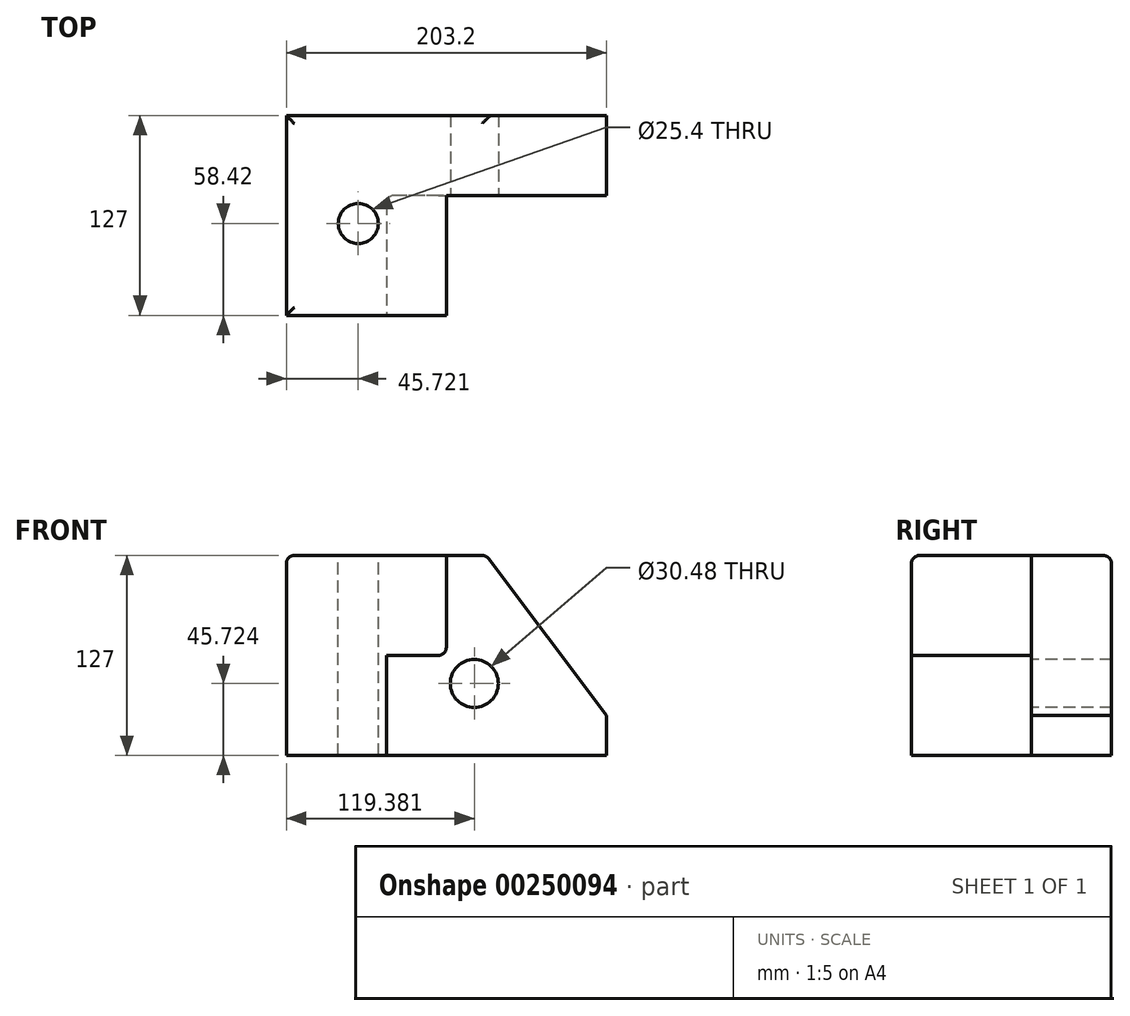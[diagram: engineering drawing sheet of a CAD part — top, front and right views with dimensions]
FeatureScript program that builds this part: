
annotation { "Feature Type Name" : "Feature", "Feature Type Description" : "" }
export const myFeature = defineFeature(function(context is Context, id is Id, definition is map)
    precondition{}
    {
        {
            var Q0;
            Q0=qCreatedBy(makeId("Front.planeOp"),FACE);
            var sketch = newSketch(context, id + "F0", { "sketchPlane" : qUnion([Q0])});
            skLineSegment(sketch, "E0.bottom", {"start": v(67.15, -74.26) * mm, "end": v(-136.05, -74.26) * mm});
            skLineSegment(sketch, "E0.top", {"start": v(67.15, 52.74) * mm, "end": v(-136.05, 52.74) * mm});
            skLineSegment(sketch, "E0.left", {"start": v(67.15, -74.26) * mm, "end": v(67.15, 52.74) * mm});
            skLineSegment(sketch, "E0.right", {"start": v(-136.05, -74.26) * mm, "end": v(-136.05, 52.74) * mm});
            skPoint(sketch, "E0.middle", {"position": v(-34.45, -10.76) * mm});
            skSolve(sketch);
        }
        {
            var Q0;
            Q0 = qSketchRegion(id + "F0", true);
            var Q1;
            Q1 = qConstructionFilter(qBodyType(qCreatedBy(id + "F0" ,EDGE), BodyType.WIRE), ConstructionObject.NO);
            extrude(context, id + "F1", {"entities" : qUnion([Q0]), "surfaceEntities" : qUnion([Q1]), "depth" : 127 * mm});
        }
        {
            var Q0;
            Q0=makeQuery(id+"F1.opExtrude","CAP_FACE",FACE,{"disambiguationData":[OSD([sQuery(id+"F0.wireOp",EDGE,"E0.bottom"),sQuery(id+"F0.wireOp",EDGE,"E0.top"),sQuery(id+"F0.wireOp",EDGE,"E0.left"),sQuery(id+"F0.wireOp",EDGE,"E0.right")])],"isStart":false});
            var sketch = newSketch(context, id + "F2", { "sketchPlane" : qUnion([Q0])});
            skLineSegment(sketch, "E1", {"start": v(-34.45, 52.74) * mm, "end": v(-34.45, -10.76) * mm});
            skLineSegment(sketch, "E2", {"start": v(-34.45, -10.76) * mm, "end": v(-72.55, -10.76) * mm});
            skLineSegment(sketch, "E3", {"start": v(-72.55, -10.76) * mm, "end": v(-72.55, -74.26) * mm});
            skLineSegment(sketch, "E4", {"start": v(-136.05, 52.74) * mm, "end": v(-34.45, 52.74) * mm});
            skLineSegment(sketch, "E5", {"start": v(-72.55, -74.26) * mm, "end": v(-136.05, -74.26) * mm});
            skSolve(sketch);
        }
        {
            var Q0;
            {var subQ3=sQuery(id+"F2.wireOp",EDGE,"E1");Q0=makeQuery(id+"F2.imprint","IMPRINT",FACE,{"disambiguationData":[TD([[makeQuery(id+"F2.imprint","IMPRINT",EDGE,{"derivedFrom":subQ3}),1.0]])]});}
            extrude(context, id + "F3", {"entities" : qUnion([Q0]), "operationType" : NewBodyOperationType.REMOVE, "oppositeDirection" : true, "depth" : 76.2 * mm});
        }
        {
            var Q0;
            Q0=makeQuery(id+"F1.opExtrude","SWEPT_EDGE",EDGE,{"disambiguationData":[OSD([sQuery(id+"F0.wireOp",EDGE,"E0.top"),sQuery(id+"F0.wireOp",EDGE,"E0.left")])]});
            chamfer(context, id + "F4", {"entities" : qUnion([Q0]), "chamferType" : ChamferType.TWO_OFFSETS, "width1" : 76.2 * mm, "oppositeDirection" : false, "width2" : 101.6 * mm, "tangentPropagation" : true});
        }
        {
            var Q0;
            Q0=makeQuery(id+"F1.opExtrude","SWEPT_EDGE",EDGE,{"disambiguationData":[OSD([sQuery(id+"F0.wireOp",EDGE,"E0.top"),sQuery(id+"F0.wireOp",EDGE,"E0.right")])]});
            var Q1;
            Q1=makeQuery(id+"F1.opExtrude","CAP_EDGE",EDGE,{"disambiguationData":[OSD([sQuery(id+"F0.wireOp",EDGE,"E0.top")])],"isStart":false});
            var Q2;
            Q2=makeQuery(id+"F3.boolean.opBoolean","COPY",EDGE,{"derivedFrom":makeQuery(id+"F3.opExtrude","CAP_EDGE",EDGE,{"disambiguationData":[OSD([sQuery(id+"F2.wireOp",EDGE,"E1")])],"isStart":true})});
            var Q3;
            Q3=makeQuery(id+"F3.boolean.opBoolean","COPY",EDGE,{"derivedFrom":makeQuery(id+"F3.opExtrude","CAP_EDGE",EDGE,{"disambiguationData":[OSD([sQuery(id+"F2.wireOp",EDGE,"E2")])],"isStart":true})});
            var Q4;
            Q4=makeQuery(id+"F3.boolean.opBoolean","COPY",EDGE,{"derivedFrom":makeQuery(id+"F3.opExtrude","CAP_EDGE",EDGE,{"disambiguationData":[OSD([sQuery(id+"F2.wireOp",EDGE,"E3")])],"isStart":true})});
            var Q5;
            Q5=makeQuery(id+"F3.boolean.opBoolean","COPY",EDGE,{"derivedFrom":makeQuery(id+"F3.opExtrude","CAP_EDGE",EDGE,{"disambiguationData":[OSD([sQuery(id+"F2.wireOp",EDGE,"E3")])],"isStart":false})});
            var Q6;
            Q6=makeQuery(id+"F3.boolean.opBoolean","COPY",EDGE,{"derivedFrom":makeQuery(id+"F3.opExtrude","SWEPT_EDGE",EDGE,{"disambiguationData":[OSD([sQuery(id+"F2.wireOp",EDGE,"E1"),sQuery(id+"F2.wireOp",EDGE,"E2")])]})});
            var Q7;
            Q7=makeQuery(id+"F3.boolean.opBoolean","COPY",EDGE,{"derivedFrom":makeQuery(id+"F3.opExtrude","SWEPT_EDGE",EDGE,{"disambiguationData":[OSD([sQuery(id+"F0.wireOp",EDGE,"E0.top"),sQuery(id+"F2.wireOp",EDGE,"E1"),sQuery(id+"F2.wireOp",EDGE,"E4")])]})});
            var Q8;
            Q8=makeQuery(id+"F3.boolean.opBoolean","COPY",EDGE,{"derivedFrom":makeQuery(id+"F3.opExtrude","CAP_EDGE",EDGE,{"disambiguationData":[OSD([sQuery(id+"F0.wireOp",EDGE,"E0.top")])],"isStart":false})});
            var Q9;
            Q9=makeQuery(id+"F1.opExtrude","CAP_EDGE",EDGE,{"disambiguationData":[OSD([sQuery(id+"F0.wireOp",EDGE,"E0.top")])],"isStart":true});
            var Q10;
            {var subQ0=sQuery(id+"F0.wireOp",EDGE,"E0.top");Q10=makeQuery(id+"F4.opChamfer","BLEND_EDGE",EDGE,{"blendedFrom":[makeQuery(id+"F1.opExtrude","SWEPT_EDGE",EDGE,{"disambiguationData":[OSD([subQ0,sQuery(id+"F0.wireOp",EDGE,"E0.left")])]}),makeQuery(id+"F1.opExtrude","SWEPT_FACE",FACE,{"disambiguationData":[OSD([subQ0])]})],"blendedInto":[makeQuery(id+"F1.opExtrude","SWEPT_FACE",FACE,{"disambiguationData":[OSD([subQ0])]})]});}
            fillet(context, id + "F5", {"entities" : qUnion([Q0, Q1, Q2, Q3, Q4, Q5, Q6, Q7, Q8, Q9, Q10]), "radius" : 5.08 * mm, "tangentPropagation" : true, "allowEdgeOverflow" : false});
        }
        {
            var Q0;
            Q0=makeQuery(id+"F3.boolean.opBoolean","COPY",FACE,{"derivedFrom":makeQuery(id+"F3.opExtrude","CAP_FACE",FACE,{"disambiguationData":[OSD([sQuery(id+"F0.wireOp",EDGE,"E0.bottom"),sQuery(id+"F0.wireOp",EDGE,"E0.top"),sQuery(id+"F0.wireOp",EDGE,"E0.left"),sQuery(id+"F2.wireOp",EDGE,"E1"),sQuery(id+"F2.wireOp",EDGE,"E2"),sQuery(id+"F2.wireOp",EDGE,"E3")])],"isStart":false})});
            var sketch = newSketch(context, id + "F6", { "sketchPlane" : qUnion([Q0])});
            skCircle(sketch, "E6", {"center": v(-16.67, -28.54) * mm, "radius": 15.24 * mm});
            skSolve(sketch);
        }
        {
            var Q0;
            Q0=makeQuery(id+"F6.imprint","IMPRINT",FACE,{"disambiguationData":[TD([[makeQuery(id+"F6.imprint","IMPRINT",EDGE,{"derivedFrom":sQuery(id+"F6.wireOp",EDGE,"E6")}),1.0]])]});
            var Q1;
            Q1=makeQuery(id+"F1.opExtrude","CAP_FACE",FACE,{"disambiguationData":[OSD([sQuery(id+"F0.wireOp",EDGE,"E0.bottom"),sQuery(id+"F0.wireOp",EDGE,"E0.top"),sQuery(id+"F0.wireOp",EDGE,"E0.left"),sQuery(id+"F0.wireOp",EDGE,"E0.right")])],"isStart":true});
            extrude(context, id + "F7", {"entities" : qUnion([Q0]), "operationType" : NewBodyOperationType.REMOVE, "endBound" : BoundingType.UP_TO_SURFACE, "oppositeDirection" : true, "endBoundEntityFace" : qUnion([Q1]), "depth" : 25.4 * mm});
        }
        {
            var Q0;
            Q0=makeQuery(id+"F1.opExtrude","SWEPT_FACE",FACE,{"disambiguationData":[OSD([sQuery(id+"F0.wireOp",EDGE,"E0.top")])]});
            var sketch = newSketch(context, id + "F8", { "sketchPlane" : qUnion([Q0])});
            skCircle(sketch, "E7", {"center": v(-90.33, -68.58) * mm, "radius": 12.7 * mm});
            skSolve(sketch);
        }
        {
            var Q0;
            Q0=makeQuery(id+"F8.imprint","IMPRINT",FACE,{"disambiguationData":[TD([[makeQuery(id+"F8.imprint","IMPRINT",EDGE,{"derivedFrom":sQuery(id+"F8.wireOp",EDGE,"E7")}),1.0]])]});
            var Q1;
            Q1=makeQuery(id+"F1.opExtrude","SWEPT_FACE",FACE,{"disambiguationData":[OSD([sQuery(id+"F0.wireOp",EDGE,"E0.bottom")])]});
            extrude(context, id + "F9", {"entities" : qUnion([Q0]), "operationType" : NewBodyOperationType.REMOVE, "endBound" : BoundingType.UP_TO_SURFACE, "oppositeDirection" : true, "endBoundEntityFace" : qUnion([Q1]), "depth" : 25.4 * mm});
        }
    });
